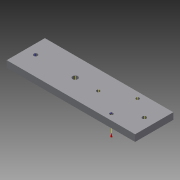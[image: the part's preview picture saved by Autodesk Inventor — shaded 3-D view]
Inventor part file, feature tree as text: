
AUTODESK INVENTOR PART (.ipt)
format: ipt  version: 2015 SP1 (Build 190203100, 203)  size: 143,872 bytes
history: native  units: mm
features: extrude x3, sketch x3, hole x2, projected_geometry x2
ambient origin geometry x8: Origin, YZ Plane, XZ Plane, XY Plane, X Axis, Y Axis, Z Axis, Center Point
bodies: Solid1 (feature_tree)
feature tree (10):
  extrude  "Extrusion1"  Depth=58.0mm
  extrude  "Extrusion2"  Depth=57.5mm
  extrude  "Extrusion3"  Depth=3.0mm
  hole  "Hole1"  [1 undecoded]
  hole  "Hole2"  [1 undecoded]
  sketch  "Sketch1"  dims[d0=115.0mm d1=58.0mm]
  sketch  "Sketch3"  dims[d2=29.0mm d3=57.5mm]
  projected_geometry  "Projected Loop2"
  sketch  "Sketch4"  dims[d4=5.0mm d5=45.0mm d6=29.0mm d7=5.0mm d8=5.0mm d9=5.0mm d11=5.0mm d13=8.0mm d14=80.0mm d15=29.0mm d16=10.0mm d17=0.0mm d18=40.0mm d19=20.0mm d20=20.0mm d21=40.0mm d22=0.0mm d23=40.0mm d24=0.0mm d25=15.0mm d26=29.0mm d27=6.0mm d28=6.0mm d29=10.0mm d30=3.0mm d31=90.0deg d32=8.0mm d33=20.594885mm d34=15.0mm d35=29.0mm d36=6.0mm d37=6.0mm d38=10.0mm d39=3.0mm d40=90.0deg d41=8.0mm d42=20.594885mm]
  projected_geometry  "Projected Loop3"
note: 2 required parameter values undecoded (feature->parameter linkage not recoverable at this tier; creation-order binding heuristic only, values carry confidence <= 0.55)
